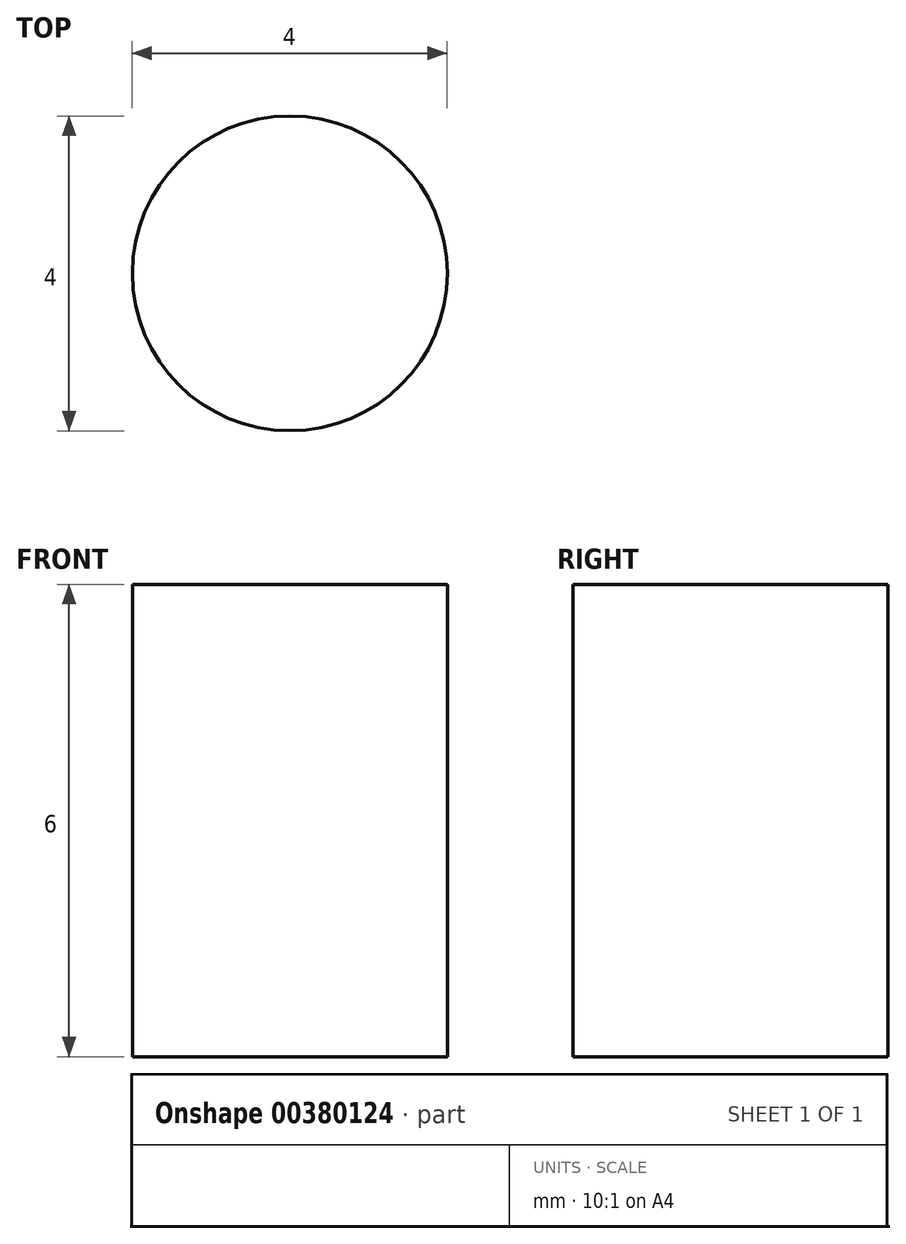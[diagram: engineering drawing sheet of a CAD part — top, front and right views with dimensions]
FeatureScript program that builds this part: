
annotation { "Feature Type Name" : "Feature", "Feature Type Description" : "" }
export const myFeature = defineFeature(function(context is Context, id is Id, definition is map)
    precondition{}
    {
        {
            var Q0;
            Q0=qCreatedBy(makeId("Top.planeOp"),FACE);
            var sketch = newSketch(context, id + "F0", { "sketchPlane" : qUnion([Q0])});
            skCircle(sketch, "E0", {"center": v(-14.13, 4.11) * mm, "radius": 2 * mm});
            skSolve(sketch);
        }
        {
            var Q0;
            Q0 = qSketchRegion(id + "F0", true);
            extrude(context, id + "F1", {"entities" : qUnion([Q0]), "depth" : 6 * mm});
        }
    });
